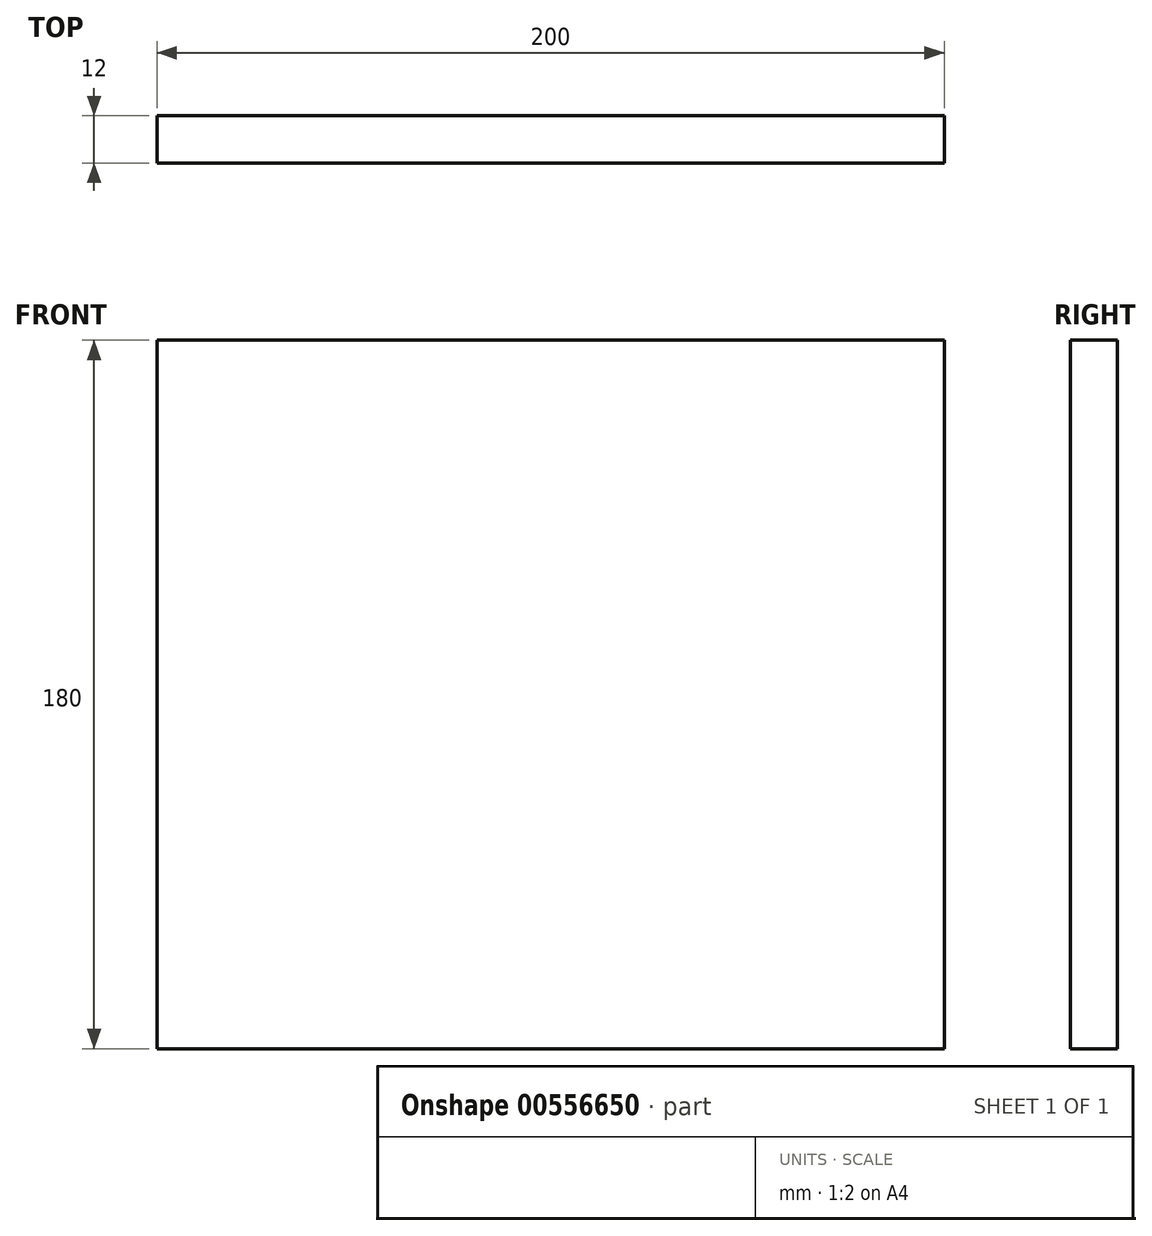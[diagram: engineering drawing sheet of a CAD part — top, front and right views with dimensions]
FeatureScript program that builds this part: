
annotation { "Feature Type Name" : "Feature", "Feature Type Description" : "" }
export const myFeature = defineFeature(function(context is Context, id is Id, definition is map)
    precondition{}
    {
        {
            var Q0;
            Q0=qCreatedBy(makeId("Front.planeOp"),FACE);
            var sketch = newSketch(context, id + "F0", { "sketchPlane" : qUnion([Q0])});
            skLineSegment(sketch, "E0", {"start": v(0, 0) * mm, "end": v(0, 180) * mm});
            skLineSegment(sketch, "E1", {"start": v(0, 180) * mm, "end": v(200, 180) * mm});
            skLineSegment(sketch, "E2", {"start": v(200, 180) * mm, "end": v(200, 0) * mm});
            skLineSegment(sketch, "E3", {"start": v(200, 0) * mm, "end": v(0, 0) * mm});
            skSolve(sketch);
        }
        {
            var Q0;
            Q0=makeQuery(id+"F0.imprint","IMPRINT",FACE,{"disambiguationData":[TD([[makeQuery(id+"F0.imprint","IMPRINT",EDGE,{"derivedFrom":sQuery(id+"F0.wireOp",EDGE,"E0")}),-1.0]])]});
            extrude(context, id + "F1", {"entities" : qUnion([Q0]), "endBound" : BoundingType.SYMMETRIC, "depth" : 12 * mm, "offsetDistance" : 25 * mm});
        }
    });
